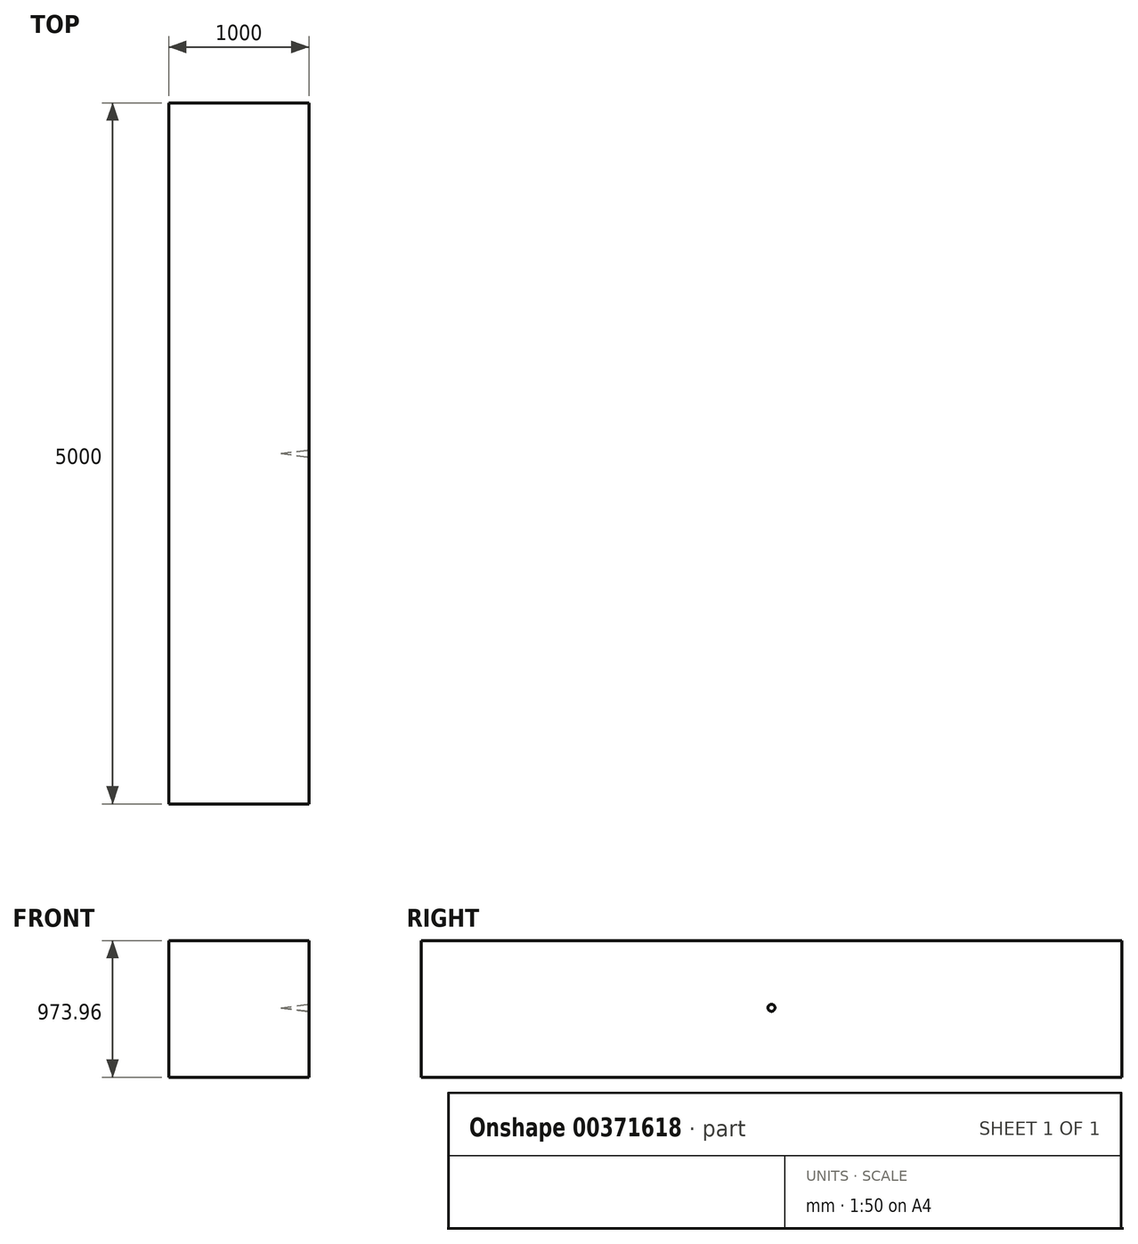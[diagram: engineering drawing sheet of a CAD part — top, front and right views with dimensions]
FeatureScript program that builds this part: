
annotation { "Feature Type Name" : "Feature", "Feature Type Description" : "" }
export const myFeature = defineFeature(function(context is Context, id is Id, definition is map)
    precondition{}
    {
        {
            var Q0;
            Q0=qCreatedBy(makeId("Front.planeOp"),FACE);
            var sketch = newSketch(context, id + "F0", { "sketchPlane" : qUnion([Q0])});
            skLineSegment(sketch, "E0.bottom", {"start": v(-494.15, 478.97) * mm, "end": v(505.85, 478.97) * mm});
            skLineSegment(sketch, "E0.top", {"start": v(-494.15, -494.99) * mm, "end": v(505.85, -494.99) * mm});
            skLineSegment(sketch, "E0.left", {"start": v(-494.15, 478.97) * mm, "end": v(-494.15, -494.99) * mm});
            skLineSegment(sketch, "E0.right", {"start": v(505.85, 478.97) * mm, "end": v(505.85, -494.99) * mm});
            skSolve(sketch);
        }
        {
            var Q0;
            Q0=makeQuery(id+"F0.imprint","IMPRINT",FACE,{"disambiguationData":[TD([[makeQuery(id+"F0.imprint","IMPRINT",EDGE,{"derivedFrom":sQuery(id+"F0.wireOp",EDGE,"E0.bottom")}),-1.0]])]});
            extrude(context, id + "F1", {"entities" : qUnion([Q0]), "depth" : 5000 * mm});
        }
        {
            var Q0;
            Q0=makeQuery(id+"F1.opExtrude","SWEPT_FACE",FACE,{"disambiguationData":[OSD([sQuery(id+"F0.wireOp",EDGE,"E0.right")])]});
            var sketch = newSketch(context, id + "F2", { "sketchPlane" : qUnion([Q0])});
            skCircle(sketch, "E1", {"center": v(-1884.9, 0) * mm, "radius": 250 * mm});
            skSolve(sketch);
        }
        {
            var Q0;
            Q0=qCreatedBy(makeId("Top.planeOp"),FACE);
            var sketch = newSketch(context, id + "F3", { "sketchPlane" : qUnion([Q0])});
            skLineSegment(sketch, "E2", {"start": v(505.85, -2500) * mm, "end": v(505.85, -2475) * mm});
            skLineSegment(sketch, "E3", {"start": v(505.85, -2475) * mm, "end": v(305.85, -2500) * mm});
            skLineSegment(sketch, "E4", {"start": v(305.85, -2500) * mm, "end": v(505.85, -2500) * mm});
            skSolve(sketch);
        }
        {
            var Q0;
            Q0 = qSketchRegion(id + "F3", true);
            var Q1;
            Q1=sQuery(id+"F3.wireOp",EDGE,"E4");
            revolve(context, id + "F4", {"operationType" : NewBodyOperationType.REMOVE, "entities" : qUnion([Q0]), "axis" : qUnion([Q1]), "revolveType" : RevolveType.FULL, "oppositeDirection" : true});
        }
    });
